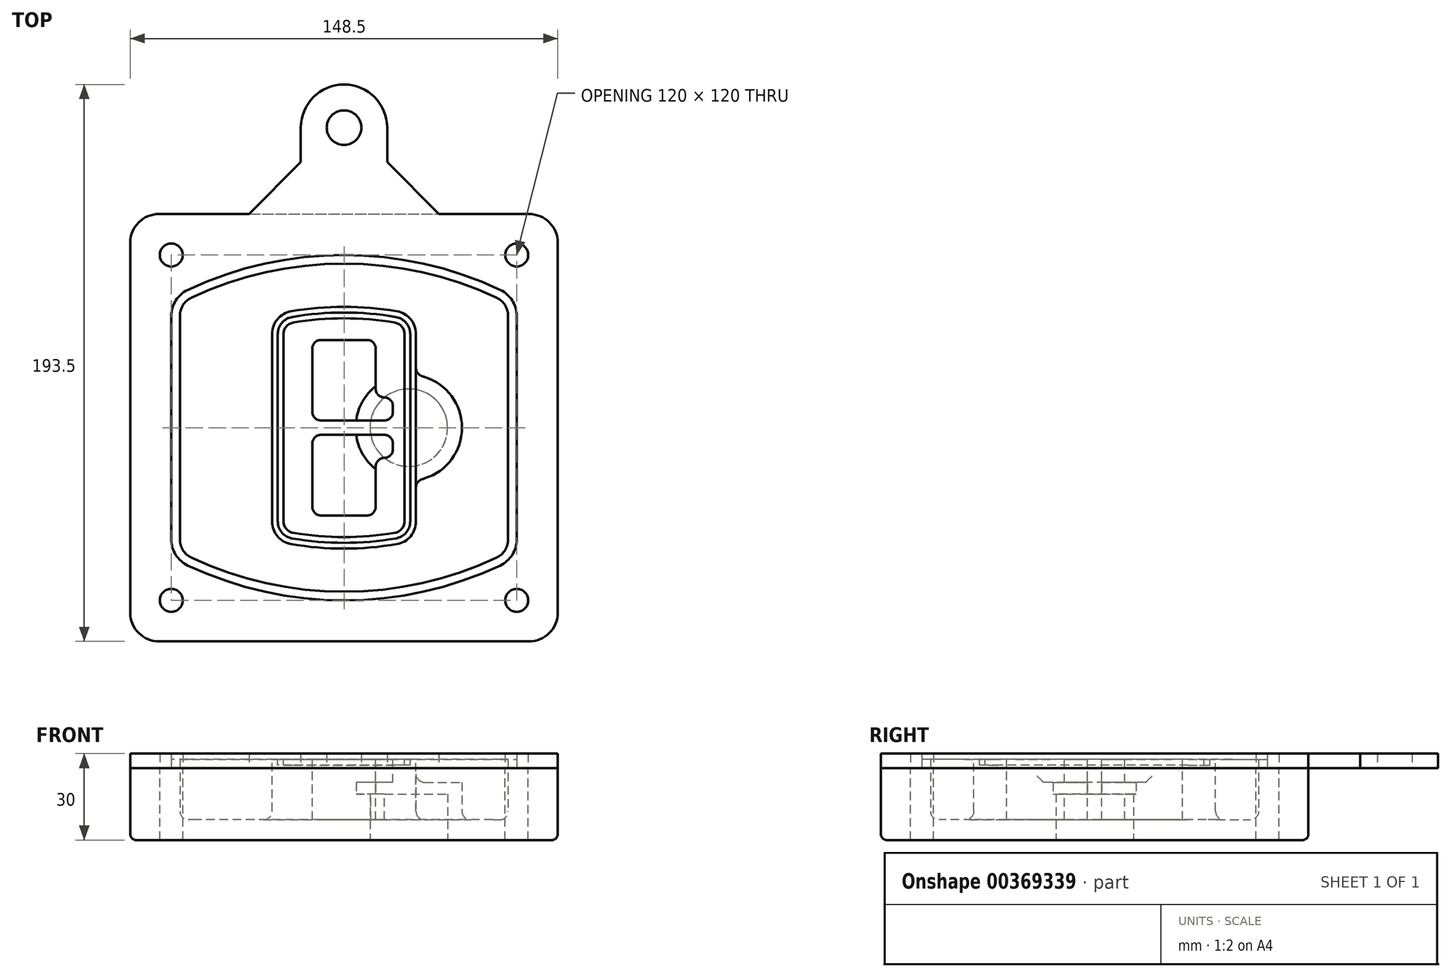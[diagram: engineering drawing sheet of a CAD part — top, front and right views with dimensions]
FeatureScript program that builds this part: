
annotation { "Feature Type Name" : "Feature", "Feature Type Description" : "" }
export const myFeature = defineFeature(function(context is Context, id is Id, definition is map)
    precondition{}
    {
        {
            var Q0;
            Q0=qCreatedBy(makeId("Top.planeOp"),FACE);
            var sketch = newSketch(context, id + "F0", { "sketchPlane" : qUnion([Q0])});
            skPoint(sketch, "E0.rect.middle", {"position": v(0, 0) * mm});
            skLineSegment(sketch, "E1.bottom", {"start": v(-64.25, -74.25) * mm, "end": v(64.25, -74.25) * mm});
            skLineSegment(sketch, "E1.top", {"start": v(-64.25, 74.25) * mm, "end": v(64.25, 74.25) * mm});
            skLineSegment(sketch, "E1.left", {"start": v(-74.25, -64.25) * mm, "end": v(-74.25, 64.25) * mm});
            skLineSegment(sketch, "E1.right", {"start": v(74.25, -64.25) * mm, "end": v(74.25, 64.25) * mm});
            skLineSegment(sketch, "E2", {"start": v(-74.25, 74.25) * mm, "end": v(74.25, -74.25) * mm, "construction": true});
            skLineSegment(sketch, "E3", {"start": v(74.25, 74.25) * mm, "end": v(-74.25, -74.25) * mm, "construction": true});
            skCircle(sketch, "E4", {"center": v(-60, 60) * mm, "radius": 4 * mm});
            skCircle(sketch, "E5", {"center": v(60, 60) * mm, "radius": 4 * mm});
            skCircle(sketch, "E6", {"center": v(60, -60) * mm, "radius": 4 * mm});
            skCircle(sketch, "E7", {"center": v(-60, -60) * mm, "radius": 4 * mm});
            skLineSegment(sketch, "E8", {"start": v(-60, 60) * mm, "end": v(60, 60) * mm, "construction": true});
            skLineSegment(sketch, "E9", {"start": v(60, 60) * mm, "end": v(60, -60) * mm, "construction": true});
            skLineSegment(sketch, "E10", {"start": v(60, -60) * mm, "end": v(-60, -60) * mm, "construction": true});
            skLineSegment(sketch, "E11", {"start": v(-60, -60) * mm, "end": v(-60, 60) * mm, "construction": true});
            skLineSegment(sketch, "E12", {"start": v(-60, 38.83) * mm, "end": v(-60, -38.83) * mm});
            skLineSegment(sketch, "E13", {"start": v(60, 38.83) * mm, "end": v(60, -38.83) * mm});
            skArc(sketch, "E14", {"start": v(54.26, 47.88) * mm, "mid": v(0, 60) * mm, "end": v(-54.26, 47.88) * mm});
            skArc(sketch, "E15", {"start": v(-54.26, -47.88) * mm, "mid": v(0, -60) * mm, "end": v(54.26, -47.88) * mm});
            skLineSegment(sketch, "E16", {"start": v(-60, 0) * mm, "end": v(60, 0) * mm, "construction": true});
            skPoint(sketch, "E17.visualSharp", {"position": v(-60, -45) * mm});
            skArc(sketch, "E17.filletArc", {"start": v(-60, -38.83) * mm, "mid": v(-58.44, -44.2) * mm, "end": v(-54.26, -47.88) * mm});
            skPoint(sketch, "E18.visualSharp", {"position": v(-60, 45) * mm});
            skArc(sketch, "E18.filletArc", {"start": v(-54.26, 47.88) * mm, "mid": v(-58.44, 44.2) * mm, "end": v(-60, 38.83) * mm});
            skPoint(sketch, "E19.visualSharp", {"position": v(60, 45) * mm});
            skArc(sketch, "E19.filletArc", {"start": v(60, 38.83) * mm, "mid": v(58.44, 44.2) * mm, "end": v(54.26, 47.88) * mm});
            skPoint(sketch, "E20.visualSharp", {"position": v(60, -45) * mm});
            skArc(sketch, "E20.filletArc", {"start": v(54.26, -47.88) * mm, "mid": v(58.44, -44.2) * mm, "end": v(60, -38.83) * mm});
            skPoint(sketch, "E21.visualSharp", {"position": v(-74.25, 74.25) * mm});
            skArc(sketch, "E21.filletArc", {"start": v(-64.25, 74.25) * mm, "mid": v(-71.32, 71.32) * mm, "end": v(-74.25, 64.25) * mm});
            skPoint(sketch, "E22.visualSharp", {"position": v(74.25, 74.25) * mm});
            skArc(sketch, "E22.filletArc", {"start": v(74.25, 64.25) * mm, "mid": v(71.32, 71.32) * mm, "end": v(64.25, 74.25) * mm});
            skPoint(sketch, "E23.visualSharp", {"position": v(74.25, -74.25) * mm});
            skArc(sketch, "E23.filletArc", {"start": v(64.25, -74.25) * mm, "mid": v(71.32, -71.32) * mm, "end": v(74.25, -64.25) * mm});
            skPoint(sketch, "E24.visualSharp", {"position": v(-74.25, -74.25) * mm});
            skArc(sketch, "E24.filletArc", {"start": v(-74.25, -64.25) * mm, "mid": v(-71.32, -71.32) * mm, "end": v(-64.25, -74.25) * mm});
            skArc(sketch, "E25.0", {"start": v(57, 38.83) * mm, "mid": v(55.9, 42.58) * mm, "end": v(52.98, 45.17) * mm});
            skLineSegment(sketch, "E25.1", {"start": v(57, 38.83) * mm, "end": v(57, -38.83) * mm});
            skArc(sketch, "E25.2", {"start": v(52.98, -45.17) * mm, "mid": v(55.9, -42.58) * mm, "end": v(57, -38.83) * mm});
            skArc(sketch, "E25.3", {"start": v(-52.98, -45.17) * mm, "mid": v(0, -57) * mm, "end": v(52.98, -45.17) * mm});
            skArc(sketch, "E25.4", {"start": v(-57, -38.83) * mm, "mid": v(-55.9, -42.58) * mm, "end": v(-52.98, -45.17) * mm});
            skArc(sketch, "E25.5", {"start": v(52.98, 45.17) * mm, "mid": v(0, 57) * mm, "end": v(-52.98, 45.17) * mm});
            skLineSegment(sketch, "E25.6", {"start": v(-57, 38.83) * mm, "end": v(-57, -38.83) * mm});
            skArc(sketch, "E25.7", {"start": v(-52.98, 45.17) * mm, "mid": v(-55.9, 42.58) * mm, "end": v(-57, 38.83) * mm});
            skArc(sketch, "E26.0", {"start": v(-55.96, 51.5) * mm, "mid": v(-61.82, 46.33) * mm, "end": v(-64, 38.83) * mm});
            skArc(sketch, "E26.1", {"start": v(55.96, 51.5) * mm, "mid": v(0, 64) * mm, "end": v(-55.96, 51.5) * mm});
            skArc(sketch, "E26.2", {"start": v(64, 38.83) * mm, "mid": v(61.82, 46.33) * mm, "end": v(55.96, 51.5) * mm});
            skLineSegment(sketch, "E26.3", {"start": v(64, 38.83) * mm, "end": v(64, -38.83) * mm});
            skArc(sketch, "E26.4", {"start": v(55.96, -51.5) * mm, "mid": v(61.82, -46.33) * mm, "end": v(64, -38.83) * mm});
            skLineSegment(sketch, "E26.5", {"start": v(-64, 38.83) * mm, "end": v(-64, -38.83) * mm});
            skArc(sketch, "E26.6", {"start": v(-55.96, -51.5) * mm, "mid": v(0, -64) * mm, "end": v(55.96, -51.5) * mm});
            skArc(sketch, "E26.7", {"start": v(-64, -38.83) * mm, "mid": v(-61.82, -46.33) * mm, "end": v(-55.96, -51.5) * mm});
            skSolve(sketch);
        }
        {
            var Q0;
            Q0=makeQuery(id+"F0.imprint","IMPRINT",FACE,{"disambiguationData":[TD([[makeQuery(id+"F0.imprint","IMPRINT",EDGE,{"derivedFrom":sQuery(id+"F0.wireOp",EDGE,"E1.bottom")}),1.0]])]});
            var Q1;
            Q1=makeQuery(id+"F0.imprint","IMPRINT",FACE,{"disambiguationData":[TD([[makeQuery(id+"F0.imprint","IMPRINT",EDGE,{"derivedFrom":sQuery(id+"F0.wireOp",EDGE,"E12")}),1.0]])]});
            var Q2;
            Q2=makeQuery(id+"F0.imprint","IMPRINT",FACE,{"disambiguationData":[TD([[makeQuery(id+"F0.imprint","IMPRINT",EDGE,{"derivedFrom":sQuery(id+"F0.wireOp",EDGE,"E25.0")}),1.0]])]});
            var Q3;
            Q3=makeQuery(id+"F0.imprint","IMPRINT",FACE,{"disambiguationData":[TD([[makeQuery(id+"F0.imprint","IMPRINT",EDGE,{"derivedFrom":sQuery(id+"F0.wireOp",EDGE,"E12")}),-1.0]])]});
            extrude(context, id + "F1", {"entities" : qUnion([Q0, Q1, Q2, Q3]), "oppositeDirection" : true, "depth" : 25 * mm});
        }
        {
            var Q0;
            Q0=makeQuery(id+"F0.imprint","IMPRINT",FACE,{"disambiguationData":[TD([[makeQuery(id+"F0.imprint","IMPRINT",EDGE,{"derivedFrom":sQuery(id+"F0.wireOp",EDGE,"E12")}),1.0]])]});
            extrude(context, id + "F2", {"entities" : qUnion([Q0]), "operationType" : NewBodyOperationType.ADD, "depth" : 3 * mm});
        }
        {
            var Q0;
            Q0=makeQuery(id+"F0.imprint","IMPRINT",FACE,{"disambiguationData":[TD([[makeQuery(id+"F0.imprint","IMPRINT",EDGE,{"derivedFrom":sQuery(id+"F0.wireOp",EDGE,"E25.0")}),1.0]])]});
            extrude(context, id + "F3", {"entities" : qUnion([Q0]), "operationType" : NewBodyOperationType.REMOVE, "oppositeDirection" : true, "depth" : 18 * mm});
        }
        {
            var Q0;
            Q0=makeQuery(id+"F2.opExtrude","CAP_FACE",FACE,{"disambiguationData":[OSD([sQuery(id+"F0.wireOp",EDGE,"E12"),sQuery(id+"F0.wireOp",EDGE,"E13"),sQuery(id+"F0.wireOp",EDGE,"E14"),sQuery(id+"F0.wireOp",EDGE,"E15"),sQuery(id+"F0.wireOp",EDGE,"E17.filletArc"),sQuery(id+"F0.wireOp",EDGE,"E18.filletArc"),sQuery(id+"F0.wireOp",EDGE,"E19.filletArc"),sQuery(id+"F0.wireOp",EDGE,"E20.filletArc"),sQuery(id+"F0.wireOp",EDGE,"E25.0"),sQuery(id+"F0.wireOp",EDGE,"E25.1"),sQuery(id+"F0.wireOp",EDGE,"E25.2"),sQuery(id+"F0.wireOp",EDGE,"E25.3"),sQuery(id+"F0.wireOp",EDGE,"E25.4"),sQuery(id+"F0.wireOp",EDGE,"E25.5"),sQuery(id+"F0.wireOp",EDGE,"E25.6"),sQuery(id+"F0.wireOp",EDGE,"E25.7")])],"isStart":false});
            var sketch = newSketch(context, id + "F4", { "sketchPlane" : qUnion([Q0])});
            skArc(sketch, "E27.0", {"start": v(-18.34, -40.45) * mm, "mid": v(0, -42) * mm, "end": v(18.34, -40.45) * mm});
            skArc(sketch, "E28.0", {"start": v(18.34, 40.45) * mm, "mid": v(0, 42) * mm, "end": v(-18.34, 40.45) * mm});
            skLineSegment(sketch, "E29", {"start": v(-25, 32.57) * mm, "end": v(-25, -32.57) * mm});
            skLineSegment(sketch, "E30", {"start": v(25, 32.57) * mm, "end": v(25, -32.57) * mm});
            skLineSegment(sketch, "E31", {"start": v(-25, 39.1) * mm, "end": v(25, 39.1) * mm, "construction": true});
            skLineSegment(sketch, "E32", {"start": v(-25, -39.1) * mm, "end": v(25, -39.1) * mm, "construction": true});
            skPoint(sketch, "E33.visualSharp", {"position": v(-25, 39.1) * mm});
            skArc(sketch, "E33.filletArc", {"start": v(-18.34, 40.45) * mm, "mid": v(-23.11, 37.73) * mm, "end": v(-25, 32.57) * mm});
            skPoint(sketch, "E34.visualSharp", {"position": v(25, 39.1) * mm});
            skArc(sketch, "E34.filletArc", {"start": v(25, 32.57) * mm, "mid": v(23.11, 37.73) * mm, "end": v(18.34, 40.45) * mm});
            skPoint(sketch, "E35.visualSharp", {"position": v(25, -39.1) * mm});
            skArc(sketch, "E35.filletArc", {"start": v(18.34, -40.45) * mm, "mid": v(23.11, -37.73) * mm, "end": v(25, -32.57) * mm});
            skPoint(sketch, "E36.visualSharp", {"position": v(-25, -39.1) * mm});
            skArc(sketch, "E36.filletArc", {"start": v(-25, -32.57) * mm, "mid": v(-23.11, -37.73) * mm, "end": v(-18.34, -40.45) * mm});
            skArc(sketch, "E37.0", {"start": v(52.98, 45.17) * mm, "mid": v(0, 57) * mm, "end": v(-52.98, 45.17) * mm});
            skArc(sketch, "E37.1", {"start": v(-52.98, 45.17) * mm, "mid": v(-55.9, 42.58) * mm, "end": v(-57, 38.83) * mm});
            skLineSegment(sketch, "E37.2", {"start": v(-57, 38.83) * mm, "end": v(-57, -38.83) * mm});
            skArc(sketch, "E37.3", {"start": v(-57, -38.83) * mm, "mid": v(-55.9, -42.58) * mm, "end": v(-52.98, -45.17) * mm});
            skArc(sketch, "E37.4", {"start": v(-52.98, -45.17) * mm, "mid": v(0, -57) * mm, "end": v(52.98, -45.17) * mm});
            skArc(sketch, "E37.5", {"start": v(52.98, -45.17) * mm, "mid": v(55.9, -42.58) * mm, "end": v(57, -38.83) * mm});
            skLineSegment(sketch, "E37.6", {"start": v(57, 38.83) * mm, "end": v(57, -38.83) * mm});
            skArc(sketch, "E37.7", {"start": v(57, 38.83) * mm, "mid": v(55.9, 42.58) * mm, "end": v(52.98, 45.17) * mm});
            skLineSegment(sketch, "E38.0", {"start": v(23, 32.57) * mm, "end": v(23, -32.57) * mm});
            skArc(sketch, "E38.1", {"start": v(18, -38.48) * mm, "mid": v(21.58, -36.44) * mm, "end": v(23, -32.57) * mm});
            skArc(sketch, "E38.2", {"start": v(-18, -38.48) * mm, "mid": v(0, -40) * mm, "end": v(18, -38.48) * mm});
            skArc(sketch, "E38.3", {"start": v(-23, -32.57) * mm, "mid": v(-21.58, -36.44) * mm, "end": v(-18, -38.48) * mm});
            skLineSegment(sketch, "E38.4", {"start": v(-23, 32.57) * mm, "end": v(-23, -32.57) * mm});
            skArc(sketch, "E38.5", {"start": v(23, 32.57) * mm, "mid": v(21.58, 36.44) * mm, "end": v(18, 38.48) * mm});
            skArc(sketch, "E38.6", {"start": v(-18, 38.48) * mm, "mid": v(-21.58, 36.44) * mm, "end": v(-23, 32.57) * mm});
            skArc(sketch, "E38.7", {"start": v(18, 38.48) * mm, "mid": v(0, 40) * mm, "end": v(-18, 38.48) * mm});
            skArc(sketch, "E39.0", {"start": v(21, 32.57) * mm, "mid": v(20.06, 35.15) * mm, "end": v(17.67, 36.5) * mm});
            skLineSegment(sketch, "E39.1", {"start": v(21, 32.57) * mm, "end": v(21, -32.57) * mm});
            skArc(sketch, "E39.2", {"start": v(17.67, -36.5) * mm, "mid": v(20.06, -35.15) * mm, "end": v(21, -32.57) * mm});
            skArc(sketch, "E39.3", {"start": v(-17.67, -36.5) * mm, "mid": v(0, -38) * mm, "end": v(17.67, -36.5) * mm});
            skArc(sketch, "E39.4", {"start": v(-21, -32.57) * mm, "mid": v(-20.06, -35.15) * mm, "end": v(-17.67, -36.5) * mm});
            skArc(sketch, "E39.5", {"start": v(17.67, 36.5) * mm, "mid": v(0, 38) * mm, "end": v(-17.67, 36.5) * mm});
            skLineSegment(sketch, "E39.6", {"start": v(-21, 32.57) * mm, "end": v(-21, -32.57) * mm});
            skArc(sketch, "E39.7", {"start": v(-17.67, 36.5) * mm, "mid": v(-20.06, 35.15) * mm, "end": v(-21, 32.57) * mm});
            skLineSegment(sketch, "E40", {"start": v(-25, 0) * mm, "end": v(25, 0) * mm, "construction": true});
            skLineSegment(sketch, "E41", {"start": v(-11, 5.5) * mm, "end": v(-11, 27.5) * mm});
            skLineSegment(sketch, "E42", {"start": v(-8, 30.5) * mm, "end": v(8, 30.5) * mm});
            skLineSegment(sketch, "E43", {"start": v(11, 27.5) * mm, "end": v(11, 13.5) * mm});
            skLineSegment(sketch, "E44", {"start": v(14, 10.5) * mm, "end": v(14, 10.5) * mm});
            skLineSegment(sketch, "E45", {"start": v(17, 7.5) * mm, "end": v(17, 5.5) * mm});
            skLineSegment(sketch, "E46", {"start": v(14, 2.5) * mm, "end": v(-8, 2.5) * mm});
            skPoint(sketch, "E47.visualSharp", {"position": v(-11, 30.5) * mm});
            skArc(sketch, "E47.filletArc", {"start": v(-8, 30.5) * mm, "mid": v(-10.12, 29.62) * mm, "end": v(-11, 27.5) * mm});
            skPoint(sketch, "E48.visualSharp", {"position": v(11, 30.5) * mm});
            skArc(sketch, "E48.filletArc", {"start": v(11, 27.5) * mm, "mid": v(10.12, 29.62) * mm, "end": v(8, 30.5) * mm});
            skPoint(sketch, "E49.visualSharp", {"position": v(11, 10.5) * mm});
            skArc(sketch, "E49.filletArc", {"start": v(11, 13.5) * mm, "mid": v(11.88, 11.38) * mm, "end": v(14, 10.5) * mm});
            skPoint(sketch, "E50.visualSharp", {"position": v(17, 10.5) * mm});
            skArc(sketch, "E50.filletArc", {"start": v(17, 7.5) * mm, "mid": v(16.12, 9.62) * mm, "end": v(14, 10.5) * mm});
            skPoint(sketch, "E51.visualSharp", {"position": v(17, 2.5) * mm});
            skArc(sketch, "E51.filletArc", {"start": v(14, 2.5) * mm, "mid": v(16.12, 3.38) * mm, "end": v(17, 5.5) * mm});
            skPoint(sketch, "E52.visualSharp", {"position": v(-11, 2.5) * mm});
            skArc(sketch, "E52.filletArc", {"start": v(-11, 5.5) * mm, "mid": v(-10.12, 3.38) * mm, "end": v(-8, 2.5) * mm});
            skLineSegment(sketch, "E53.0.MirrorCS", {"start": v(14, -2.5) * mm, "end": v(-8, -2.5) * mm});
            skArc(sketch, "E54.0.MirrorCS", {"start": v(-11, -5.5) * mm, "mid": v(-10.12, -3.38) * mm, "end": v(-8, -2.5) * mm});
            skLineSegment(sketch, "E55.0.MirrorCS", {"start": v(-11, -5.5) * mm, "end": v(-11, -27.5) * mm});
            skArc(sketch, "E56.0.MirrorCS", {"start": v(-8, -30.5) * mm, "mid": v(-10.12, -29.62) * mm, "end": v(-11, -27.5) * mm});
            skLineSegment(sketch, "E57.0.MirrorCS", {"start": v(-8, -30.5) * mm, "end": v(8, -30.5) * mm});
            skArc(sketch, "E58.0.MirrorCS", {"start": v(11, -27.5) * mm, "mid": v(10.12, -29.62) * mm, "end": v(8, -30.5) * mm});
            skLineSegment(sketch, "E59.0.MirrorCS", {"start": v(11, -27.5) * mm, "end": v(11, -13.5) * mm});
            skArc(sketch, "E60.0.MirrorCS", {"start": v(11, -13.5) * mm, "mid": v(11.88, -11.38) * mm, "end": v(14, -10.5) * mm});
            skArc(sketch, "E61.0.MirrorCS", {"start": v(17, -7.5) * mm, "mid": v(16.12, -9.62) * mm, "end": v(14, -10.5) * mm});
            skLineSegment(sketch, "E62.0.MirrorCS", {"start": v(17, -7.5) * mm, "end": v(17, -5.5) * mm});
            skArc(sketch, "E63.0.MirrorCS", {"start": v(14, -2.5) * mm, "mid": v(16.12, -3.38) * mm, "end": v(17, -5.5) * mm});
            skSolve(sketch);
        }
        {
            var Q0;
            Q0=makeQuery(id+"F4.imprint","IMPRINT",FACE,{"disambiguationData":[TD([[makeQuery(id+"F4.imprint","IMPRINT",EDGE,{"derivedFrom":sQuery(id+"F4.wireOp",EDGE,"E27.0")}),1.0]])]});
            var Q1;
            Q1=makeQuery(id+"F4.imprint","IMPRINT",FACE,{"disambiguationData":[TD([[makeQuery(id+"F4.imprint","IMPRINT",EDGE,{"derivedFrom":sQuery(id+"F4.wireOp",EDGE,"E38.0")}),-1.0]])]});
            var Q2;
            Q2=makeQuery(id+"F4.imprint","IMPRINT",FACE,{"disambiguationData":[TD([[makeQuery(id+"F4.imprint","IMPRINT",EDGE,{"derivedFrom":sQuery(id+"F4.wireOp",EDGE,"E39.0")}),1.0]])]});
            extrude(context, id + "F5", {"entities" : qUnion([Q0, Q1, Q2]), "operationType" : NewBodyOperationType.ADD, "endBound" : BoundingType.UP_TO_NEXT, "oppositeDirection" : true, "depth" : 25 * mm});
        }
        {
            var Q0;
            Q0=makeQuery(id+"F4.imprint","IMPRINT",FACE,{"disambiguationData":[TD([[makeQuery(id+"F4.imprint","IMPRINT",EDGE,{"derivedFrom":sQuery(id+"F4.wireOp",EDGE,"E38.0")}),-1.0]])]});
            extrude(context, id + "F6", {"entities" : qUnion([Q0]), "operationType" : NewBodyOperationType.REMOVE, "oppositeDirection" : true, "depth" : 2 * mm});
        }
        {
            var Q0;
            Q0=makeQuery(id+"F1.opExtrude","CAP_FACE",FACE,{"disambiguationData":[OSD([sQuery(id+"F0.wireOp",EDGE,"E1.bottom"),sQuery(id+"F0.wireOp",EDGE,"E1.top"),sQuery(id+"F0.wireOp",EDGE,"E1.left"),sQuery(id+"F0.wireOp",EDGE,"E1.right"),sQuery(id+"F0.wireOp",EDGE,"E4"),sQuery(id+"F0.wireOp",EDGE,"E5"),sQuery(id+"F0.wireOp",EDGE,"E6"),sQuery(id+"F0.wireOp",EDGE,"E7"),sQuery(id+"F0.wireOp",EDGE,"E21.filletArc"),sQuery(id+"F0.wireOp",EDGE,"E22.filletArc"),sQuery(id+"F0.wireOp",EDGE,"E23.filletArc"),sQuery(id+"F0.wireOp",EDGE,"E24.filletArc")])],"isStart":false});
            var sketch = newSketch(context, id + "F7", { "sketchPlane" : qUnion([Q0])});
            skCircle(sketch, "E64", {"center": v(22.5, 0) * mm, "radius": 13.47 * mm});
            skCircle(sketch, "E65", {"center": v(-39.81, 0) * mm, "radius": 13.47 * mm});
            skLineSegment(sketch, "E66", {"start": v(74.25, 0) * mm, "end": v(-74.25, 0) * mm});
            skCircle(sketch, "E67", {"center": v(22.5, 0) * mm, "radius": 18.47 * mm});
            skCircle(sketch, "E68", {"center": v(60, -60) * mm, "radius": 6 * mm});
            skCircle(sketch, "E69", {"center": v(-60, -60) * mm, "radius": 6 * mm});
            skCircle(sketch, "E70", {"center": v(-60, 60) * mm, "radius": 6 * mm});
            skCircle(sketch, "E71", {"center": v(60, 60) * mm, "radius": 6 * mm});
            skSolve(sketch);
        }
        {
            var Q0;
            {var subQ1=sQuery(id+"F7.wireOp",EDGE,"E66");var subQ4=sQuery(id+"F7.wireOp",EDGE,"E64");var subQ6=makeQuery(id+"F7.imprint","INTERSECT",VERTEX,{"disambiguationData":[OD(0.0)],"derivedFrom":[subQ4,subQ1]});Q0=makeQuery(id+"F7.imprint","IMPRINT",FACE,{"disambiguationData":[TD([[makeQuery(id+"F7.imprint","IMPRINT",EDGE,{"disambiguationData":[TD([[subQ6,-1.0]])],"derivedFrom":subQ4}),-1.0]])]});}
            var Q1;
            {var subQ0=sQuery(id+"F7.wireOp",EDGE,"E66");var subQ1=sQuery(id+"F7.wireOp",EDGE,"E64");var subQ3=makeQuery(id+"F7.imprint","INTERSECT",VERTEX,{"disambiguationData":[OD(0.0)],"derivedFrom":[subQ1,subQ0]});Q1=makeQuery(id+"F7.imprint","IMPRINT",FACE,{"disambiguationData":[TD([[makeQuery(id+"F7.imprint","IMPRINT",EDGE,{"disambiguationData":[TD([[subQ3,-1.0]])],"derivedFrom":subQ1}),1.0]])]});}
            var Q2;
            {var subQ0=sQuery(id+"F7.wireOp",EDGE,"E66");var subQ1=sQuery(id+"F7.wireOp",EDGE,"E64");var subQ3=makeQuery(id+"F7.imprint","INTERSECT",VERTEX,{"disambiguationData":[OD(0.0)],"derivedFrom":[subQ1,subQ0]});Q2=makeQuery(id+"F7.imprint","IMPRINT",FACE,{"disambiguationData":[TD([[makeQuery(id+"F7.imprint","IMPRINT",EDGE,{"disambiguationData":[TD([[subQ3,1.0]])],"derivedFrom":subQ1}),1.0]])]});}
            var Q3;
            {var subQ1=sQuery(id+"F7.wireOp",EDGE,"E66");var subQ4=sQuery(id+"F7.wireOp",EDGE,"E64");var subQ6=makeQuery(id+"F7.imprint","INTERSECT",VERTEX,{"disambiguationData":[OD(0.0)],"derivedFrom":[subQ4,subQ1]});Q3=makeQuery(id+"F7.imprint","IMPRINT",FACE,{"disambiguationData":[TD([[makeQuery(id+"F7.imprint","IMPRINT",EDGE,{"disambiguationData":[TD([[subQ6,1.0]])],"derivedFrom":subQ4}),-1.0]])]});}
            extrude(context, id + "F8", {"entities" : qUnion([Q0, Q1, Q2, Q3]), "operationType" : NewBodyOperationType.ADD, "oppositeDirection" : true, "depth" : 20 * mm});
        }
        {
            var Q0;
            {var subQ0=sQuery(id+"F7.wireOp",EDGE,"E66");var subQ1=sQuery(id+"F7.wireOp",EDGE,"E64");var subQ3=makeQuery(id+"F7.imprint","INTERSECT",VERTEX,{"disambiguationData":[OD(0.0)],"derivedFrom":[subQ1,subQ0]});Q0=makeQuery(id+"F7.imprint","IMPRINT",FACE,{"disambiguationData":[TD([[makeQuery(id+"F7.imprint","IMPRINT",EDGE,{"disambiguationData":[TD([[subQ3,-1.0]])],"derivedFrom":subQ1}),1.0]])]});}
            var Q1;
            {var subQ0=sQuery(id+"F7.wireOp",EDGE,"E66");var subQ1=sQuery(id+"F7.wireOp",EDGE,"E64");var subQ3=makeQuery(id+"F7.imprint","INTERSECT",VERTEX,{"disambiguationData":[OD(0.0)],"derivedFrom":[subQ1,subQ0]});Q1=makeQuery(id+"F7.imprint","IMPRINT",FACE,{"disambiguationData":[TD([[makeQuery(id+"F7.imprint","IMPRINT",EDGE,{"disambiguationData":[TD([[subQ3,1.0]])],"derivedFrom":subQ1}),1.0]])]});}
            extrude(context, id + "F9", {"entities" : qUnion([Q0, Q1]), "operationType" : NewBodyOperationType.REMOVE, "oppositeDirection" : true, "depth" : 16 * mm});
        }
        {
            var Q0;
            Q0=makeQuery(id+"F9.boolean.opBoolean","COPY",FACE,{"derivedFrom":makeQuery(id+"F9.opExtrude","CAP_FACE",FACE,{"disambiguationData":[OSD([sQuery(id+"F7.wireOp",EDGE,"E64")])],"isStart":false})});
            var sketch = newSketch(context, id + "F10", { "sketchPlane" : qUnion([Q0])});
            skArc(sketch, "E72.0", {"start": v(11, 14.45) * mm, "mid": v(6.45, 9.13) * mm, "end": v(4.2, 2.5) * mm});
            skArc(sketch, "E72.1", {"start": v(4.2, -2.5) * mm, "mid": v(6.45, -9.13) * mm, "end": v(11, -14.45) * mm});
            skLineSegment(sketch, "E73", {"start": v(4.2, -2.5) * mm, "end": v(14, -2.5) * mm});
            skLineSegment(sketch, "E74.0", {"start": v(14, 2.5) * mm, "end": v(4.2, 2.5) * mm});
            skArc(sketch, "E74.1", {"start": v(14, 2.5) * mm, "mid": v(16.12, 3.38) * mm, "end": v(17, 5.5) * mm});
            skLineSegment(sketch, "E74.2", {"start": v(17, 7.5) * mm, "end": v(17, 5.5) * mm});
            skArc(sketch, "E74.3", {"start": v(17, 7.5) * mm, "mid": v(16.12, 9.62) * mm, "end": v(14, 10.5) * mm});
            skArc(sketch, "E74.4", {"start": v(11, 13.5) * mm, "mid": v(11.88, 11.38) * mm, "end": v(14, 10.5) * mm});
            skLineSegment(sketch, "E74.5", {"start": v(11, 14.45) * mm, "end": v(11, 13.5) * mm});
            skLineSegment(sketch, "E74.7", {"start": v(14, -2.5) * mm, "end": v(4.2, -2.5) * mm});
            skArc(sketch, "E74.8", {"start": v(14, -2.5) * mm, "mid": v(16.12, -3.38) * mm, "end": v(17, -5.5) * mm});
            skLineSegment(sketch, "E74.9", {"start": v(17, -7.5) * mm, "end": v(17, -5.5) * mm});
            skArc(sketch, "E74.10", {"start": v(17, -7.5) * mm, "mid": v(16.12, -9.62) * mm, "end": v(14, -10.5) * mm});
            skArc(sketch, "E74.11", {"start": v(11, -13.5) * mm, "mid": v(11.88, -11.38) * mm, "end": v(14, -10.5) * mm});
            skLineSegment(sketch, "E74.12", {"start": v(11, -14.45) * mm, "end": v(11, -13.5) * mm});
            skPoint(sketch, "E75.orphan", {"position": v(11, -27.5) * mm});
            skPoint(sketch, "E76.orphan", {"position": v(-8, -2.5) * mm});
            skPoint(sketch, "E77.orphan", {"position": v(-8, 2.5) * mm});
            skPoint(sketch, "E78.orphan", {"position": v(11, 27.5) * mm});
            skSolve(sketch);
        }
        {
            var Q0;
            {var subQ7=sQuery(id+"F10.wireOp",EDGE,"E72.0");var subQ14=sQuery(id+"F10.wireOp",EDGE,"E72.1");var subQ16=sQuery(id+"F10.wireOp",EDGE,"E74.1");var subQ18=sQuery(id+"F10.wireOp",EDGE,"E74.8");Q0=qUnion([makeQuery(id+"F10.imprint","IMPRINT",FACE,{"disambiguationData":[TD([[makeQuery(id+"F10.imprint","IMPRINT",EDGE,{"derivedFrom":subQ7}),1.0]])]}),makeQuery(id+"F10.imprint","IMPRINT",FACE,{"disambiguationData":[TD([[makeQuery(id+"F10.imprint","IMPRINT",EDGE,{"derivedFrom":subQ14}),1.0]])]}),makeQuery(id+"F10.imprint","IMPRINT",FACE,{"disambiguationData":[TD([[makeQuery(id+"F10.imprint","IMPRINT",EDGE,{"derivedFrom":subQ16}),1.0]])]}),makeQuery(id+"F10.imprint","IMPRINT",FACE,{"disambiguationData":[TD([[makeQuery(id+"F10.imprint","IMPRINT",EDGE,{"derivedFrom":subQ18}),-1.0]])]})]);}
            var Q1;
            Q1=makeQuery(id+"F5.boolean.opBoolean","SPLIT",FACE,{"disambiguationData":[TD([makeQuery(id+"F5.opExtrude","SWEPT_FACE",FACE,{"disambiguationData":[OSD([sQuery(id+"F4.wireOp",EDGE,"E41")])]})])],"derivedFrom":makeQuery(id+"F3.boolean.opBoolean","COPY",FACE,{"derivedFrom":makeQuery(id+"F3.opExtrude","CAP_FACE",FACE,{"disambiguationData":[OSD([sQuery(id+"F0.wireOp",EDGE,"E25.0"),sQuery(id+"F0.wireOp",EDGE,"E25.1"),sQuery(id+"F0.wireOp",EDGE,"E25.2"),sQuery(id+"F0.wireOp",EDGE,"E25.3"),sQuery(id+"F0.wireOp",EDGE,"E25.4"),sQuery(id+"F0.wireOp",EDGE,"E25.5"),sQuery(id+"F0.wireOp",EDGE,"E25.6"),sQuery(id+"F0.wireOp",EDGE,"E25.7")])],"isStart":false})})});
            extrude(context, id + "F11", {"entities" : qUnion([Q0]), "operationType" : NewBodyOperationType.REMOVE, "endBound" : BoundingType.UP_TO_SURFACE, "endBoundEntityFace" : qUnion([Q1]), "depth" : 25 * mm});
        }
        {
            var Q0;
            Q0=makeQuery(id+"F3.boolean.opBoolean","COPY",EDGE,{"derivedFrom":makeQuery(id+"F3.opExtrude","CAP_EDGE",EDGE,{"disambiguationData":[OSD([sQuery(id+"F0.wireOp",EDGE,"E25.6")])],"isStart":false})});
            var Q1;
            Q1=makeQuery(id+"F8.boolean.opBoolean","INTERSECT",EDGE,{"derivedFrom":[makeQuery(id+"F5.opExtrude","SWEPT_FACE",FACE,{"disambiguationData":[OSD([sQuery(id+"F4.wireOp",EDGE,"E30")])]}),makeQuery(id+"F8.opExtrude","CAP_FACE",FACE,{"disambiguationData":[OSD([sQuery(id+"F7.wireOp",EDGE,"E67")])],"isStart":false})]});
            var Q2;
            Q2=makeQuery(id+"F8.boolean.opBoolean","INTERSECT",EDGE,{"disambiguationData":[OD(1.0)],"derivedFrom":[makeQuery(id+"F5.opExtrude","SWEPT_FACE",FACE,{"disambiguationData":[OSD([sQuery(id+"F4.wireOp",EDGE,"E30")])]}),makeQuery(id+"F8.opExtrude","SWEPT_FACE",FACE,{"disambiguationData":[OSD([sQuery(id+"F7.wireOp",EDGE,"E67")])]})]});
            var Q3;
            {var subQ0=sQuery(id+"F4.wireOp",EDGE,"E30");Q3=makeQuery(id+"F8.boolean.opBoolean","SPLIT",EDGE,{"disambiguationData":[TD([makeQuery(id+"F5.opExtrude","SWEPT_FACE",FACE,{"disambiguationData":[OSD([sQuery(id+"F4.wireOp",EDGE,"E35.filletArc")])]})])],"derivedFrom":makeQuery(id+"F5.opExtrude","CAP_EDGE",EDGE,{"disambiguationData":[OSD([subQ0])],"isStart":false})});}
            var Q4;
            {var subQ0=sQuery(id+"F0.wireOp",EDGE,"E25.7");var subQ1=sQuery(id+"F0.wireOp",EDGE,"E25.1");var subQ2=sQuery(id+"F0.wireOp",EDGE,"E25.6");var subQ3=sQuery(id+"F0.wireOp",EDGE,"E25.5");var subQ4=sQuery(id+"F0.wireOp",EDGE,"E25.4");var subQ5=sQuery(id+"F0.wireOp",EDGE,"E25.0");var subQ6=sQuery(id+"F0.wireOp",EDGE,"E25.2");var subQ7=sQuery(id+"F0.wireOp",EDGE,"E25.3");Q4=makeQuery(id+"F8.boolean.opBoolean","INTERSECT",EDGE,{"derivedFrom":[makeQuery(id+"F5.boolean.opBoolean","SPLIT",FACE,{"disambiguationData":[TD([makeQuery(id+"F2.opExtrude","SWEPT_FACE",FACE,{"disambiguationData":[OSD([subQ5])]})])],"derivedFrom":makeQuery(id+"F3.boolean.opBoolean","COPY",FACE,{"derivedFrom":makeQuery(id+"F3.opExtrude","CAP_FACE",FACE,{"disambiguationData":[OSD([subQ5,subQ1,subQ6,subQ7,subQ4,subQ3,subQ2,subQ0])],"isStart":false})})}),makeQuery(id+"F8.opExtrude","SWEPT_FACE",FACE,{"disambiguationData":[OSD([sQuery(id+"F7.wireOp",EDGE,"E67")])]})]});}
            var Q5;
            Q5=makeQuery(id+"F8.boolean.opBoolean","INTERSECT",EDGE,{"disambiguationData":[OD(0.0)],"derivedFrom":[makeQuery(id+"F5.opExtrude","SWEPT_FACE",FACE,{"disambiguationData":[OSD([sQuery(id+"F4.wireOp",EDGE,"E30")])]}),makeQuery(id+"F8.opExtrude","SWEPT_FACE",FACE,{"disambiguationData":[OSD([sQuery(id+"F7.wireOp",EDGE,"E67")])]})]});
            fillet(context, id + "F12", {"entities" : qUnion([Q0, Q1, Q2, Q3, Q4, Q5]), "radius" : 3 * mm, "tangentPropagation" : true, "allowEdgeOverflow" : false});
        }
        {
            var Q0;
            Q0=makeQuery(id+"F1.opExtrude","CAP_EDGE",EDGE,{"disambiguationData":[OSD([sQuery(id+"F0.wireOp",EDGE,"E1.bottom")])],"isStart":false});
            fillet(context, id + "F13", {"entities" : qUnion([Q0]), "radius" : 2 * mm, "tangentPropagation" : true, "allowEdgeOverflow" : false});
        }
        {
            var Q0;
            {var subQ0=sQuery(id+"F0.wireOp",EDGE,"E21.filletArc");var subQ1=sQuery(id+"F0.wireOp",EDGE,"E7");var subQ2=sQuery(id+"F0.wireOp",EDGE,"E6");var subQ3=sQuery(id+"F0.wireOp",EDGE,"E5");var subQ4=sQuery(id+"F0.wireOp",EDGE,"E4");var subQ5=sQuery(id+"F0.wireOp",EDGE,"E22.filletArc");var subQ6=sQuery(id+"F0.wireOp",EDGE,"E1.bottom");var subQ7=sQuery(id+"F0.wireOp",EDGE,"E1.right");var subQ8=sQuery(id+"F0.wireOp",EDGE,"E1.top");var subQ9=sQuery(id+"F0.wireOp",EDGE,"E1.left");var subQ10=sQuery(id+"F0.wireOp",EDGE,"E23.filletArc");var subQ11=sQuery(id+"F0.wireOp",EDGE,"E24.filletArc");Q0=makeQuery(id+"F2.boolean.opBoolean","SPLIT",FACE,{"disambiguationData":[TD([makeQuery(id+"F1.opExtrude","SWEPT_FACE",FACE,{"disambiguationData":[OSD([subQ6])]})])],"derivedFrom":makeQuery(id+"F1.opExtrude","CAP_FACE",FACE,{"disambiguationData":[OSD([subQ6,subQ8,subQ9,subQ7,subQ4,subQ3,subQ2,subQ1,subQ0,subQ5,subQ10,subQ11])],"isStart":true})});}
            var sketch = newSketch(context, id + "F14", { "sketchPlane" : qUnion([Q0])});
            skLineSegment(sketch, "E79", {"start": v(0, 74.25) * mm, "end": v(0, 104.25) * mm, "construction": true});
            skCircle(sketch, "E80", {"center": v(0, 104.25) * mm, "radius": 6 * mm});
            skArc(sketch, "E81", {"start": v(15, 104.25) * mm, "mid": v(0, 119.25) * mm, "end": v(-15, 104.25) * mm});
            skLineSegment(sketch, "E82", {"start": v(-15, 104.25) * mm, "end": v(-15, 92.25) * mm});
            skLineSegment(sketch, "E83", {"start": v(15, 92.25) * mm, "end": v(15, 104.25) * mm});
            skLineSegment(sketch, "E84", {"start": v(15, 92.25) * mm, "end": v(33, 74.25) * mm});
            skLineSegment(sketch, "E85", {"start": v(-15, 92.25) * mm, "end": v(-33, 74.25) * mm});
            skPoint(sketch, "E86.endSnap0", {"position": v(60, 0) * mm});
            skLineSegment(sketch, "E87", {"start": v(79.77, 0) * mm, "end": v(-74.25, 0) * mm, "construction": true});
            skArc(sketch, "E88.MirrorCS", {"start": v(-15, 104.25) * mm, "mid": v(0, 119.25) * mm, "end": v(15, 104.25) * mm});
            skLineSegment(sketch, "E89.MirrorCS", {"start": v(-15, 92.25) * mm, "end": v(-15, 104.25) * mm});
            skLineSegment(sketch, "E90.MirrorCS", {"start": v(15, 104.25) * mm, "end": v(15, 92.25) * mm});
            skArc(sketch, "E91.MirrorCS", {"start": v(15, -104.25) * mm, "mid": v(0, -119.25) * mm, "end": v(-15, -104.25) * mm});
            skLineSegment(sketch, "E92.MirrorCS", {"start": v(15, -104.25) * mm, "end": v(15, -92.25) * mm});
            skLineSegment(sketch, "E93.MirrorCS", {"start": v(15, -92.25) * mm, "end": v(15, -104.25) * mm});
            skLineSegment(sketch, "E94.MirrorCS", {"start": v(-15, -92.25) * mm, "end": v(-33, -74.25) * mm});
            skCircle(sketch, "E95.MirrorC", {"center": v(0, -104.25) * mm, "radius": 6 * mm});
            skLineSegment(sketch, "E96.MirrorCS", {"start": v(15, -92.25) * mm, "end": v(33, -74.25) * mm});
            skLineSegment(sketch, "E97.MirrorCS", {"start": v(-15, -104.25) * mm, "end": v(-15, -92.25) * mm});
            skLineSegment(sketch, "E98.MirrorCS", {"start": v(0, -74.25) * mm, "end": v(0, -104.25) * mm, "construction": true});
            skLineSegment(sketch, "E99.MirrorCS", {"start": v(-15, -92.25) * mm, "end": v(-15, -104.25) * mm});
            skArc(sketch, "E100.MirrorCS", {"start": v(-15, -104.25) * mm, "mid": v(0, -119.25) * mm, "end": v(15, -104.25) * mm});
            skSolve(sketch);
        }
        {
            var Q0;
            {var subQ0=sQuery(id+"F14.wireOp",EDGE,"E85");Q0=makeQuery(id+"F14.imprint","IMPRINT",FACE,{"disambiguationData":[TD([[makeQuery(id+"F14.imprint","IMPRINT",EDGE,{"derivedFrom":subQ0}),1.0]])]});}
            var Q1;
            Q1=makeQuery(id+"F14.imprint","IMPRINT",FACE,{"disambiguationData":[TD([[makeQuery(id+"F14.imprint","IMPRINT",EDGE,{"derivedFrom":sQuery(id+"F14.wireOp",EDGE,"E95.MirrorC")}),-1.0]])]});
            var Q2;
            Q2=makeQuery(id+"F14.imprint","IMPRINT",FACE,{"disambiguationData":[TD([[makeQuery(id+"F14.imprint","IMPRINT",EDGE,{"derivedFrom":makeQuery(id+"F1.opExtrude","CAP_EDGE",EDGE,{"disambiguationData":[OSD([sQuery(id+"F0.wireOp",EDGE,"E1.left")])],"isStart":true})}),-1.0]])]});
            extrude(context, id + "F15", {"entities" : qUnion([Q0, Q1, Q2]), "depth" : 5 * mm});
        }
    });
